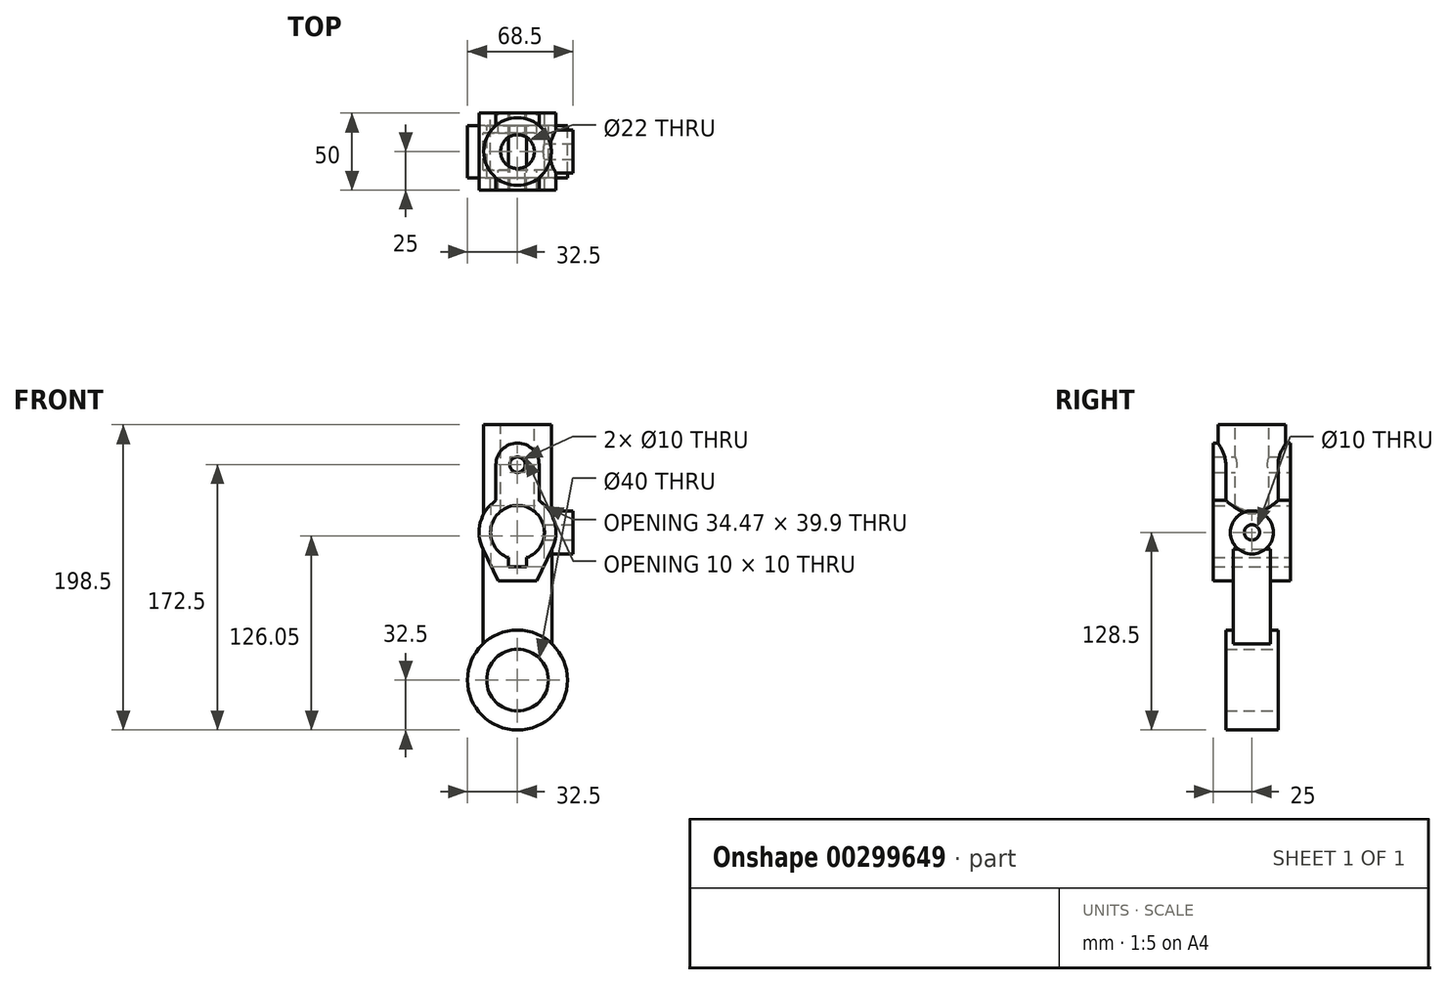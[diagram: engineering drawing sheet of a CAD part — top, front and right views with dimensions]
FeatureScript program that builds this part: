
annotation { "Feature Type Name" : "Feature", "Feature Type Description" : "" }
export const myFeature = defineFeature(function(context is Context, id is Id, definition is map)
    precondition{}
    {
        {
            var Q0;
            Q0=qCreatedBy(makeId("Front.planeOp"),FACE);
            var sketch = newSketch(context, id + "F0", { "sketchPlane" : qUnion([Q0])});
            skCircle(sketch, "E0", {"center": v(0, 0) * mm, "radius": 20 * mm});
            skCircle(sketch, "E1", {"center": v(0, 0) * mm, "radius": 32.5 * mm});
            skLineSegment(sketch, "E2", {"start": v(0, 0) * mm, "end": v(0, 194.34) * mm, "construction": true});
            skLineSegment(sketch, "E3", {"start": v(-22.5, 23.45) * mm, "end": v(-22.5, 96) * mm});
            skLineSegment(sketch, "E4", {"start": v(22.5, 96) * mm, "end": v(22.5, 23.45) * mm});
            skLineSegment(sketch, "E5", {"start": v(-22.5, 96) * mm, "end": v(22.5, 96) * mm});
            skArc(sketch, "E6", {"start": v(6, 79.56) * mm, "mid": v(0, 113.5) * mm, "end": v(-6, 79.56) * mm});
            skLineSegment(sketch, "E7.top", {"start": v(-6, 73.6) * mm, "end": v(6, 73.6) * mm});
            skLineSegment(sketch, "E7.left", {"start": v(-6, 79.56) * mm, "end": v(-6, 73.6) * mm});
            skLineSegment(sketch, "E7.right", {"start": v(6, 79.56) * mm, "end": v(6, 73.6) * mm});
            skLineSegment(sketch, "E8", {"start": v(-22.5, 85.1) * mm, "end": v(-12.5, 64.46) * mm});
            skLineSegment(sketch, "E9", {"start": v(22.5, 85.1) * mm, "end": v(12.5, 64.46) * mm});
            skArc(sketch, "E10.trimOffspring", {"start": v(22.5, 85.1) * mm, "mid": v(0, 121) * mm, "end": v(-22.5, 85.1) * mm});
            skLineSegment(sketch, "E11", {"start": v(-12.5, 64.46) * mm, "end": v(12.5, 64.46) * mm});
            skLineSegment(sketch, "E12.left", {"start": v(-14, 140) * mm, "end": v(-14, 116.71) * mm});
            skLineSegment(sketch, "E12.right", {"start": v(14, 140) * mm, "end": v(14, 116.71) * mm});
            skArc(sketch, "E13", {"start": v(14, 140) * mm, "mid": v(0, 154) * mm, "end": v(-14, 140) * mm});
            skCircle(sketch, "E14", {"center": v(0, 140) * mm, "radius": 5 * mm});
            skSolve(sketch);
        }
        {
            var Q0;
            Q0=makeQuery(id+"F0.imprint","IMPRINT",FACE,{"disambiguationData":[TD([[makeQuery(id+"F0.imprint","IMPRINT",EDGE,{"derivedFrom":sQuery(id+"F0.wireOp",EDGE,"E0")}),-1.0]])]});
            extrude(context, id + "F1", {"entities" : qUnion([Q0]), "endBound" : BoundingType.SYMMETRIC, "depth" : 34 * mm});
        }
        {
            var Q0;
            {var subQ0=sQuery(id+"F0.wireOp",EDGE,"E3");Q0=makeQuery(id+"F0.imprint","IMPRINT",FACE,{"disambiguationData":[TD([[makeQuery(id+"F0.imprint","IMPRINT",EDGE,{"derivedFrom":subQ0}),-1.0]])]});}
            extrude(context, id + "F2", {"entities" : qUnion([Q0]), "operationType" : NewBodyOperationType.ADD, "endBound" : BoundingType.SYMMETRIC, "depth" : 24 * mm});
        }
        {
            var Q0;
            {var subQ5=sQuery(id+"F0.wireOp",EDGE,"E10.trimOffspring");Q0=makeQuery(id+"F0.imprint","IMPRINT",FACE,{"disambiguationData":[TD([[makeQuery(id+"F0.imprint","IMPRINT",EDGE,{"derivedFrom":subQ5}),1.0]])]});}
            var Q1;
            Q1=makeQuery(id+"F0.imprint","IMPRINT",FACE,{"disambiguationData":[TD([[makeQuery(id+"F0.imprint","IMPRINT",EDGE,{"derivedFrom":sQuery(id+"F0.wireOp",EDGE,"E7.top")}),-1.0]])]});
            var Q2;
            {var subQ1=sQuery(id+"F0.wireOp",EDGE,"E12.left");Q2=makeQuery(id+"F0.imprint","IMPRINT",FACE,{"disambiguationData":[TD([[makeQuery(id+"F0.imprint","IMPRINT",EDGE,{"derivedFrom":subQ1}),1.0]])]});}
            extrude(context, id + "F3", {"entities" : qUnion([Q0, Q1, Q2]), "operationType" : NewBodyOperationType.ADD, "endBound" : BoundingType.SYMMETRIC, "depth" : 50 * mm});
        }
        {
            var Q0;
            Q0=qCreatedBy(makeId("Right.planeOp"),FACE);
            cPlane(context, id + "F4", {"entities" : qUnion([Q0]), "cplaneType" : CPlaneType.OFFSET, "offset" : 36 * mm, "width" : 150 * mm, "height" : 150 * mm});
        }
        {
            var Q0;
            Q0=qCreatedBy(id+"F4.planeOp",FACE);
            var sketch = newSketch(context, id + "F5", { "sketchPlane" : qUnion([Q0])});
            skCircle(sketch, "E15", {"center": v(0, 96) * mm, "radius": 5 * mm});
            skCircle(sketch, "E16", {"center": v(0, 96) * mm, "radius": 14 * mm});
            skSolve(sketch);
        }
        {
            var Q0;
            Q0=makeQuery(id+"F5.imprint","IMPRINT",FACE,{"disambiguationData":[TD([[makeQuery(id+"F5.imprint","IMPRINT",EDGE,{"derivedFrom":sQuery(id+"F5.wireOp",EDGE,"E15")}),-1.0]])]});
            extrude(context, id + "F6", {"entities" : qUnion([Q0]), "operationType" : NewBodyOperationType.ADD, "endBound" : BoundingType.UP_TO_NEXT, "oppositeDirection" : true, "depth" : 25 * mm});
        }
        {
            var Q0;
            Q0=makeQuery(id+"F5.imprint","IMPRINT",FACE,{"disambiguationData":[TD([[makeQuery(id+"F5.imprint","IMPRINT",EDGE,{"derivedFrom":sQuery(id+"F5.wireOp",EDGE,"E15")}),1.0]])]});
            var Q1;
            Q1=makeQuery(id+"F3.opExtrude","SWEPT_FACE",FACE,{"disambiguationData":[OSD([sQuery(id+"F0.wireOp",EDGE,"E6")])]});
            extrude(context, id + "F7", {"entities" : qUnion([Q0]), "operationType" : NewBodyOperationType.REMOVE, "endBound" : BoundingType.UP_TO_SURFACE, "oppositeDirection" : true, "endBoundEntityFace" : qUnion([Q1]), "depth" : 25 * mm});
        }
        {
            var Q0;
            Q0=qCreatedBy(makeId("Top.planeOp"),FACE);
            cPlane(context, id + "F8", {"entities" : qUnion([Q0]), "cplaneType" : CPlaneType.OFFSET, "offset" : 166 * mm, "width" : 150 * mm, "height" : 150 * mm});
        }
        {
            var Q0;
            Q0=qCreatedBy(id+"F8.planeOp",FACE);
            var sketch = newSketch(context, id + "F9", { "sketchPlane" : qUnion([Q0])});
            skCircle(sketch, "E17", {"center": v(0, 0) * mm, "radius": 11 * mm});
            skCircle(sketch, "E18", {"center": v(0, 0) * mm, "radius": 22 * mm});
            skLineSegment(sketch, "E19.0", {"start": v(14, 25) * mm, "end": v(-14, 25) * mm});
            skLineSegment(sketch, "E20.0", {"start": v(14, -25) * mm, "end": v(-14, -25) * mm});
            skSolve(sketch);
        }
        {
            var Q0;
            Q0=makeQuery(id+"F9.imprint","IMPRINT",FACE,{"disambiguationData":[TD([[makeQuery(id+"F9.imprint","IMPRINT",EDGE,{"derivedFrom":sQuery(id+"F9.wireOp",EDGE,"E17")}),-1.0]])]});
            var Q1;
            Q1=makeQuery(id+"F9.imprint","IMPRINT",FACE,{"disambiguationData":[TD([[makeQuery(id+"F9.imprint","IMPRINT",EDGE,{"derivedFrom":sQuery(id+"F9.wireOp",EDGE,"E17")}),1.0]])]});
            extrude(context, id + "F10", {"entities" : qUnion([Q0, Q1]), "operationType" : NewBodyOperationType.ADD, "endBound" : BoundingType.UP_TO_NEXT, "oppositeDirection" : true, "depth" : 25 * mm});
        }
        {
            var Q0;
            Q0=makeQuery(id+"F9.imprint","IMPRINT",FACE,{"disambiguationData":[TD([[makeQuery(id+"F9.imprint","IMPRINT",EDGE,{"derivedFrom":sQuery(id+"F9.wireOp",EDGE,"E17")}),1.0]])]});
            var Q1;
            Q1=makeQuery(id+"F3.opExtrude","SWEPT_FACE",FACE,{"disambiguationData":[OSD([sQuery(id+"F0.wireOp",EDGE,"E6")])]});
            extrude(context, id + "F11", {"entities" : qUnion([Q0]), "operationType" : NewBodyOperationType.REMOVE, "endBound" : BoundingType.UP_TO_SURFACE, "oppositeDirection" : true, "endBoundEntityFace" : qUnion([Q1]), "depth" : 25 * mm});
        }
    });
